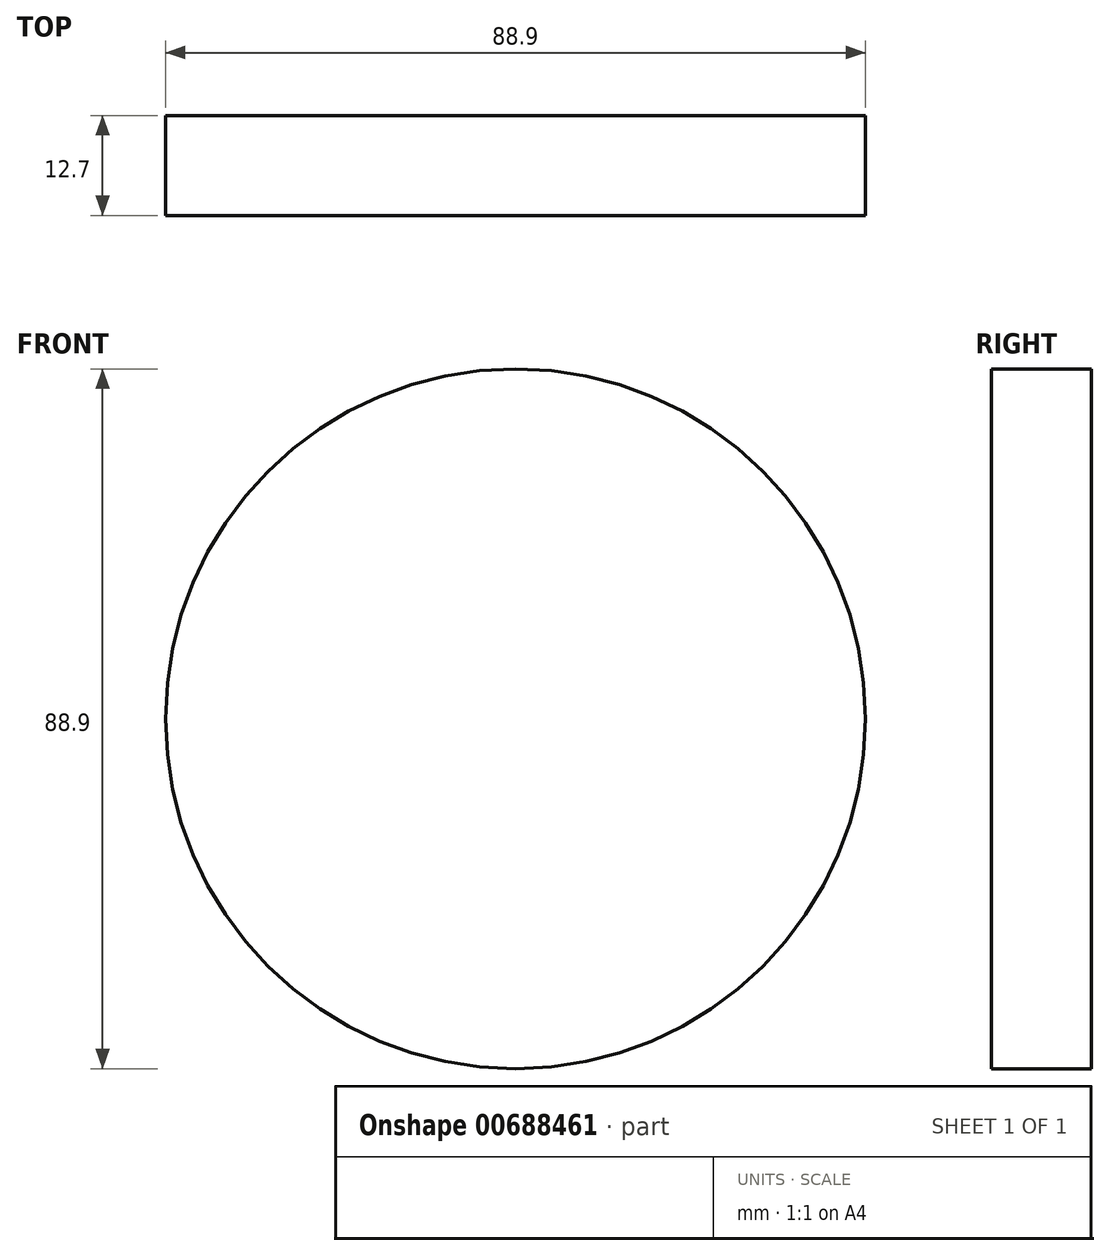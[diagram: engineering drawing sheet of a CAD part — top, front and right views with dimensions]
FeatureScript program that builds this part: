
annotation { "Feature Type Name" : "Feature", "Feature Type Description" : "" }
export const myFeature = defineFeature(function(context is Context, id is Id, definition is map)
    precondition{}
    {
        {
            var Q0;
            Q0=qCreatedBy(makeId("Front.planeOp"),FACE);
            var sketch = newSketch(context, id + "F0", { "sketchPlane" : qUnion([Q0])});
            skCircle(sketch, "E0", {"center": v(0, 0) * mm, "radius": 44.45 * mm});
            skSolve(sketch);
        }
        {
            var Q0;
            Q0=makeQuery(id+"F0.imprint","IMPRINT",FACE,{"disambiguationData":[TD([[makeQuery(id+"F0.imprint","IMPRINT",EDGE,{"derivedFrom":sQuery(id+"F0.wireOp",EDGE,"E0")}),1.0]])]});
            extrude(context, id + "F1", {"entities" : qUnion([Q0]), "oppositeDirection" : true, "depth" : 12.7 * mm, "offsetDistance" : 25.4 * mm});
        }
    });
